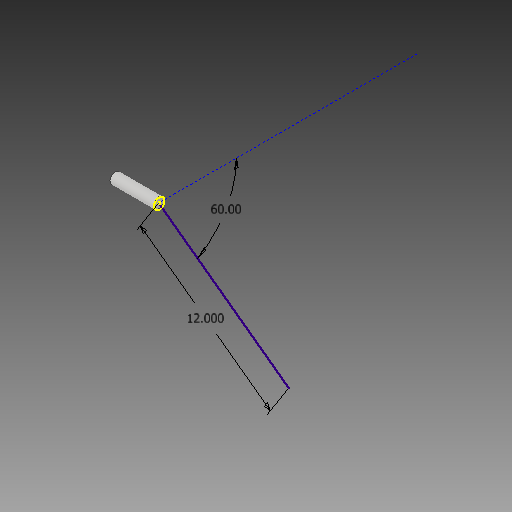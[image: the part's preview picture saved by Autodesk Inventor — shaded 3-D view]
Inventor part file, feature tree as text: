
AUTODESK INVENTOR PART (.ipt)
format: ipt  version: 2019 (Build 230136000, 136)  size: 80,896 bytes
history: native  units: in
note: dims shown in document units (in); Inventor stores cm internally (conversion verified against a paired STEP export)
features: sketch x2, extrude x1
ambient origin geometry x8: Origin, YZ Plane, XZ Plane, XY Plane, X Axis, Y Axis, Z Axis, Center Point
bodies: Solid1 (feature_tree)
feature tree (3):
  extrude  "Extrusion1"  Depth=2.0in TaperAngle=0.0deg
  sketch  "Sketch2"  dims[d3=12.0in d4=60.0deg]
  sketch  "Sketch1"  dims[d0=0.5in d1=2.0in d2=0.0in]
